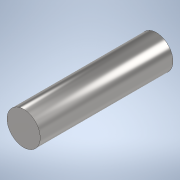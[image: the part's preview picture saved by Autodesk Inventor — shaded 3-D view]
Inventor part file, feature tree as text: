
AUTODESK INVENTOR PART (.ipt)
format: ipt  version: 2022 (Build 260153000, 153)  size: 98,304 bytes
history: native  units: in
note: dims shown in document units (in); Inventor stores cm internally (conversion verified against a paired STEP export)
features: extrude x1, sketch x1
ambient origin geometry x8: Origin, YZ Plane, XZ Plane, XY Plane, X Axis, Y Axis, Z Axis, Center Point
bodies: Solid1 (feature_tree)
feature tree (2):
  extrude  "Extrusion1"  Depth=3.1496in TaperAngle=0.0deg
  sketch  "Sketch1"  dims[d0=0.7874in d1=3.1496in d2=0.0in]
